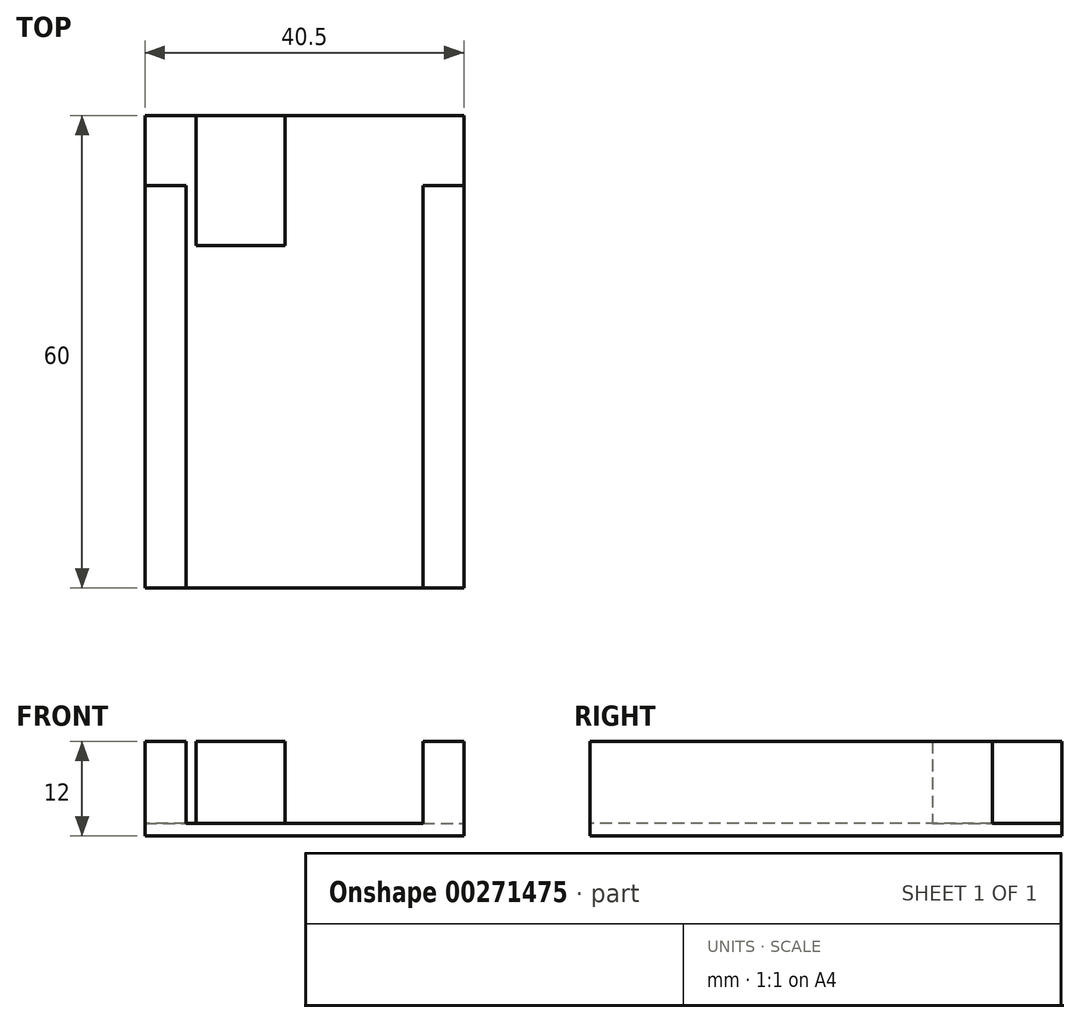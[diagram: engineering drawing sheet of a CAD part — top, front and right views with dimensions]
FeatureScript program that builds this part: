
annotation { "Feature Type Name" : "Feature", "Feature Type Description" : "" }
export const myFeature = defineFeature(function(context is Context, id is Id, definition is map)
    precondition{}
    {
        {
            var Q0;
            Q0=qCreatedBy(makeId("Top.planeOp"),FACE);
            var sketch = newSketch(context, id + "F0", { "sketchPlane" : qUnion([Q0])});
            skLineSegment(sketch, "E0.bottom", {"start": v(0, 0) * mm, "end": v(40.5, 0) * mm});
            skLineSegment(sketch, "E0.top", {"start": v(0, 60) * mm, "end": v(40.5, 60) * mm});
            skLineSegment(sketch, "E0.left", {"start": v(0, 0) * mm, "end": v(0, 60) * mm});
            skLineSegment(sketch, "E0.right", {"start": v(40.5, 0) * mm, "end": v(40.5, 60) * mm});
            skSolve(sketch);
        }
        {
            var Q0;
            Q0=makeQuery(id+"F0.imprint","IMPRINT",FACE,{"disambiguationData":[TD([[makeQuery(id+"F0.imprint","IMPRINT",EDGE,{"derivedFrom":sQuery(id+"F0.wireOp",EDGE,"E0.bottom")}),1.0]])]});
            extrude(context, id + "F1", {"entities" : qUnion([Q0]), "depth" : 1.6 * mm});
        }
        {
            var Q0;
            Q0=qCreatedBy(makeId("Top.planeOp"),FACE);
            var sketch = newSketch(context, id + "F2", { "sketchPlane" : qUnion([Q0])});
            skLineSegment(sketch, "E1.bottom", {"start": v(0, 0) * mm, "end": v(5.2, 0) * mm});
            skLineSegment(sketch, "E1.top", {"start": v(0, 51.12) * mm, "end": v(5.2, 51.12) * mm});
            skLineSegment(sketch, "E1.left", {"start": v(0, 0) * mm, "end": v(0, 51.12) * mm});
            skLineSegment(sketch, "E1.right", {"start": v(5.2, 0) * mm, "end": v(5.2, 51.12) * mm});
            skLineSegment(sketch, "E2.bottom", {"start": v(40.5, 0) * mm, "end": v(35.3, 0) * mm});
            skLineSegment(sketch, "E2.top", {"start": v(40.5, 51.12) * mm, "end": v(35.3, 51.12) * mm});
            skLineSegment(sketch, "E2.left", {"start": v(40.5, 0) * mm, "end": v(40.5, 51.12) * mm});
            skLineSegment(sketch, "E2.right", {"start": v(35.3, 0) * mm, "end": v(35.3, 51.12) * mm});
            skLineSegment(sketch, "E3.bottom", {"start": v(6.47, 60) * mm, "end": v(17.76, 60) * mm});
            skLineSegment(sketch, "E3.top", {"start": v(6.47, 43.51) * mm, "end": v(17.76, 43.51) * mm});
            skLineSegment(sketch, "E3.left", {"start": v(6.47, 60) * mm, "end": v(6.47, 43.51) * mm});
            skLineSegment(sketch, "E3.right", {"start": v(17.76, 60) * mm, "end": v(17.76, 43.51) * mm});
            skSolve(sketch);
        }
        {
            var Q0;
            Q0 = qSketchRegion(id + "F2", true);
            extrude(context, id + "F3", {"entities" : qUnion([Q0]), "operationType" : NewBodyOperationType.ADD, "depth" : 12 * mm});
        }
    });
